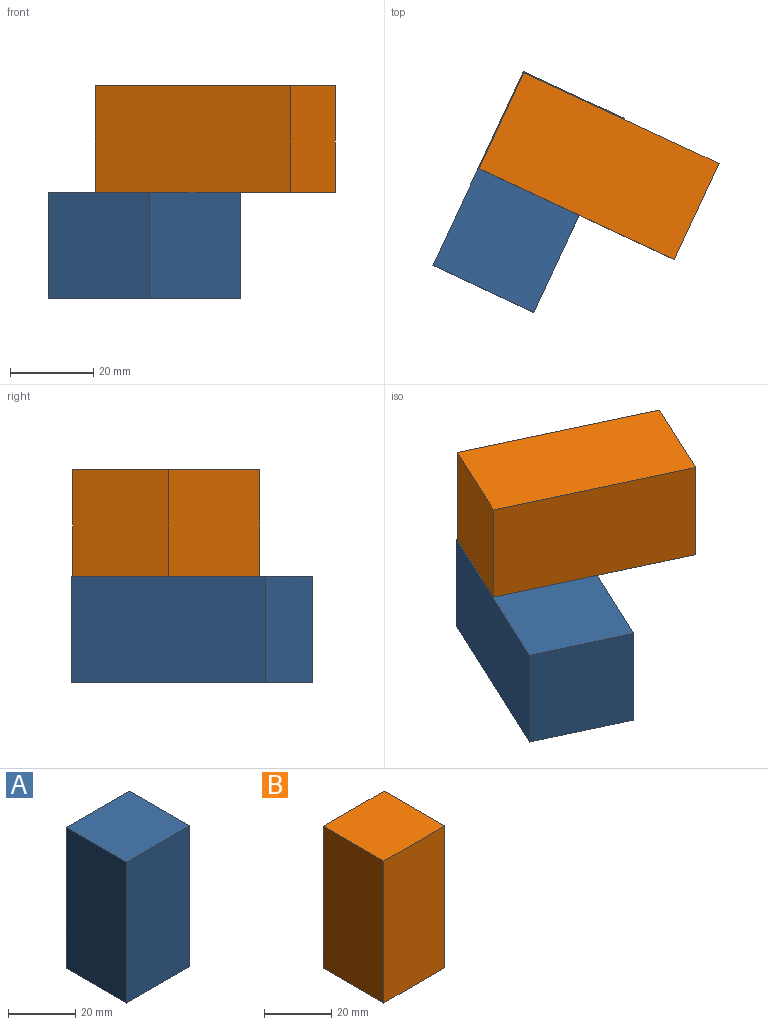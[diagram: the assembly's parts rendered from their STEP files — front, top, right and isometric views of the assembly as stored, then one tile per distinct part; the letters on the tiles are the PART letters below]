
ASSEMBLY  parts=2 mates=1
PART A: 6 faces, bbox 26.6x25.4x51.3 mm
  f0: plane 26.63x25.4mm, normal (0,0,1), area 676.5mm2, adj f1,f3,f4,f5
  f1: plane 51.26x25.4mm, normal (-1,0,0), area 1302mm2, adj f0,f2,f4,f5
  f2: plane 26.63x25.4mm, normal (0,0,-1), area 676.5mm2, adj f1,f3,f4,f5
  f3: plane 51.26x25.4mm, normal (1,0,0), area 1302mm2, adj f0,f2,f4,f5
  f4: plane 51.26x26.63mm, normal (0,-1,0), area 1365.3mm2, adj f0,f1,f2,f3
  f5: plane 51.26x26.63mm, normal (0,1,0), area 1365.3mm2, adj f0,f1,f2,f3
PART B: 6 faces, bbox 25.6x25.4x51.6 mm
  f0: plane 25.57x25.4mm, normal (0,0,1), area 649.4mm2, adj f1,f3,f4,f5
  f1: plane 51.57x25.4mm, normal (-1,0,0), area 1309.8mm2, adj f0,f2,f4,f5
  f2: plane 25.57x25.4mm, normal (0,0,-1), area 649.4mm2, adj f1,f3,f4,f5
  f3: plane 51.57x25.4mm, normal (1,0,0), area 1309.8mm2, adj f0,f2,f4,f5
  f4: plane 51.57x25.57mm, normal (0,-1,0), area 1318.5mm2, adj f0,f1,f2,f3
  f5: plane 51.57x25.57mm, normal (0,1,0), area 1318.5mm2, adj f0,f1,f2,f3
PLACE A rot(axis=(0.95,-0.21,-0.21),92.7deg) t=(50.82,-89.56,21.7)mm
PLACE B rot(axis=(-0.21,-0.95,-0.21),92.7deg) t=(-11.92,-25.6,113.23)mm
MATE fastened B.f1 <-> A.f5  axis (0,0,-1) through (-31.53,-30.47,21.7)mm
